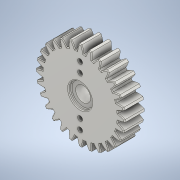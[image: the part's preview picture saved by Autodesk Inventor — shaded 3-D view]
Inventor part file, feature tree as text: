
AUTODESK INVENTOR PART (.ipt)
format: ipt  version: 2022 (Build 260153000, 153)  size: 583,168 bytes
history: native  units: mm (DEFAULTED — no unit token found)
features: sketch x5, extrude x4, plane x3, other x3, fillet x2, pattern_circular x1
ambient origin geometry x8: Origin, YZ Plane, XZ Plane, XY Plane, X Axis, Y Axis, Z Axis, Center Point
bodies: Solid1 (feature_tree)
feature tree (18):
  extrude  "Extrusion1"  Depth=10.0mm TaperAngle=0.0deg
  plane  "Work Plane2"
  plane  "Work Plane8"
  plane  "Work Plane9"
  other  "Цилиндрическое зубчатое зацепление"
  fillet  "Сопряжение1"  Radius=42.0mm
  pattern_circular  "Круговой массив1"  [2 undecoded]
  extrude  "Выдавливание2"  Depth=0.4mm TaperAngle=0.0deg
  extrude  "Выдавливание3"  TaperAngle=0.0deg  [1 undecoded]
  extrude  "Выдавливание4"  TaperAngle=0.0deg  [1 undecoded]
  fillet  "Сопряжение2"  Radius=41.3mm
  sketch  "Sketch1"  dims[d0=45.1mm d1=10.0mm d2=0.0mm d3=42.0mm]
  sketch  "Sketch2"  dims[d4=10.0mm d5=0.0mm d16=41.3mm d17=0.0mm d34=1.121997mm d39=0.0mm d41=0.0mm d43=41.3mm d46=41.3mm d47=0.0mm d48=0.0mm d49=0.4mm d50=280.0mm d51=360.0deg d53=5.0mm d54=10.0mm d55=7.6mm d56=2.5mm d57=20.0mm d59=360.0deg d61=10.0mm d62=0.0mm d63=5.2mm d64=0.1mm d65=20.0mm d67=360.0deg d69=1.5mm d70=0.0mm d71=12.0mm d72=1.5mm d73=0.0mm d74=0.4mm]
  other  "Srf1"
  sketch  "Эскиз3"
  sketch  "Эскиз4"
  sketch  "Эскиз5"
  other  "Средний диаметр"
note: 4 required parameter values undecoded (feature->parameter linkage not recoverable at this tier; creation-order binding heuristic only, values carry confidence <= 0.55)
